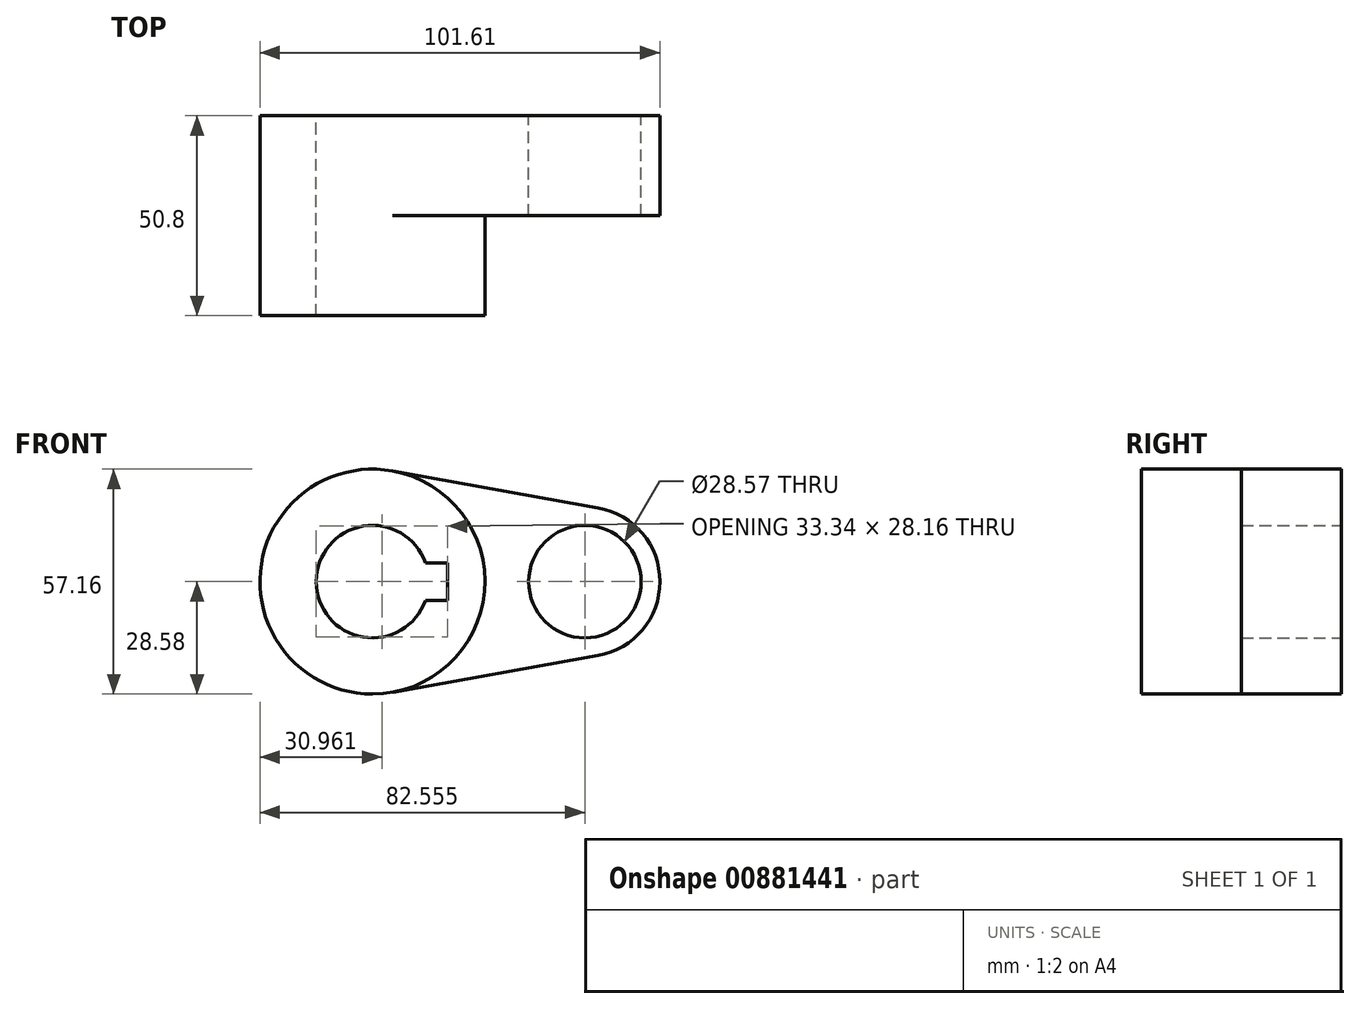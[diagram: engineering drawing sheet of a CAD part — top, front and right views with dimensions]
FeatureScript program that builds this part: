
annotation { "Feature Type Name" : "Feature", "Feature Type Description" : "" }
export const myFeature = defineFeature(function(context is Context, id is Id, definition is map)
    precondition{}
    {
        {
            var Q0;
            Q0=qCreatedBy(makeId("Front.planeOp"),FACE);
            var sketch = newSketch(context, id + "F0", { "sketchPlane" : qUnion([Q0])});
            skCircle(sketch, "E0", {"center": v(0, 0) * mm, "radius": 28.58 * mm});
            skCircle(sketch, "E1", {"center": v(53.98, 0) * mm, "radius": 19.05 * mm});
            skLineSegment(sketch, "E2", {"start": v(5.04, 28.13) * mm, "end": v(57.34, 18.75) * mm});
            skLineSegment(sketch, "E3", {"start": v(5.04, -28.13) * mm, "end": v(57.34, -18.75) * mm});
            skCircle(sketch, "E4", {"center": v(0, 0) * mm, "radius": 14.29 * mm});
            skCircle(sketch, "E5", {"center": v(53.98, 0) * mm, "radius": 14.29 * mm});
            skLineSegment(sketch, "E6.bottom", {"start": v(19.05, 4.76) * mm, "end": v(-19.05, 4.76) * mm});
            skLineSegment(sketch, "E6.top", {"start": v(19.05, -4.76) * mm, "end": v(-19.05, -4.76) * mm});
            skLineSegment(sketch, "E6.left", {"start": v(19.05, 4.76) * mm, "end": v(19.05, -4.76) * mm});
            skLineSegment(sketch, "E6.right", {"start": v(-19.05, 4.76) * mm, "end": v(-19.05, -4.76) * mm});
            skSolve(sketch);
        }
        {
            var Q0;
            Q0 = qSketchRegion(id + "F0", true);
            var Q1;
            {var subQ5=sQuery(id+"F0.wireOp",EDGE,"E6.right");Q1=makeQuery(id+"F0.imprint","IMPRINT",FACE,{"disambiguationData":[TD([[makeQuery(id+"F0.imprint","IMPRINT",EDGE,{"derivedFrom":subQ5}),1.0]])]});}
            extrude(context, id + "F1", {"entities" : qUnion([Q0, Q1]), "depth" : 25.4 * mm, "offsetDistance" : 25.4 * mm});
        }
        {
            var Q0;
            {var subQ7=sQuery(id+"F0.wireOp",EDGE,"E6.left");Q0=makeQuery(id+"F0.imprint","IMPRINT",FACE,{"disambiguationData":[TD([[makeQuery(id+"F0.imprint","IMPRINT",EDGE,{"derivedFrom":subQ7}),1.0]])]});}
            var Q1;
            {var subQ5=sQuery(id+"F0.wireOp",EDGE,"E6.right");Q1=makeQuery(id+"F0.imprint","IMPRINT",FACE,{"disambiguationData":[TD([[makeQuery(id+"F0.imprint","IMPRINT",EDGE,{"derivedFrom":subQ5}),1.0]])]});}
            extrude(context, id + "F2", {"entities" : qUnion([Q0, Q1]), "operationType" : NewBodyOperationType.ADD, "depth" : 50.8 * mm, "offsetDistance" : 25.4 * mm});
        }
    });
